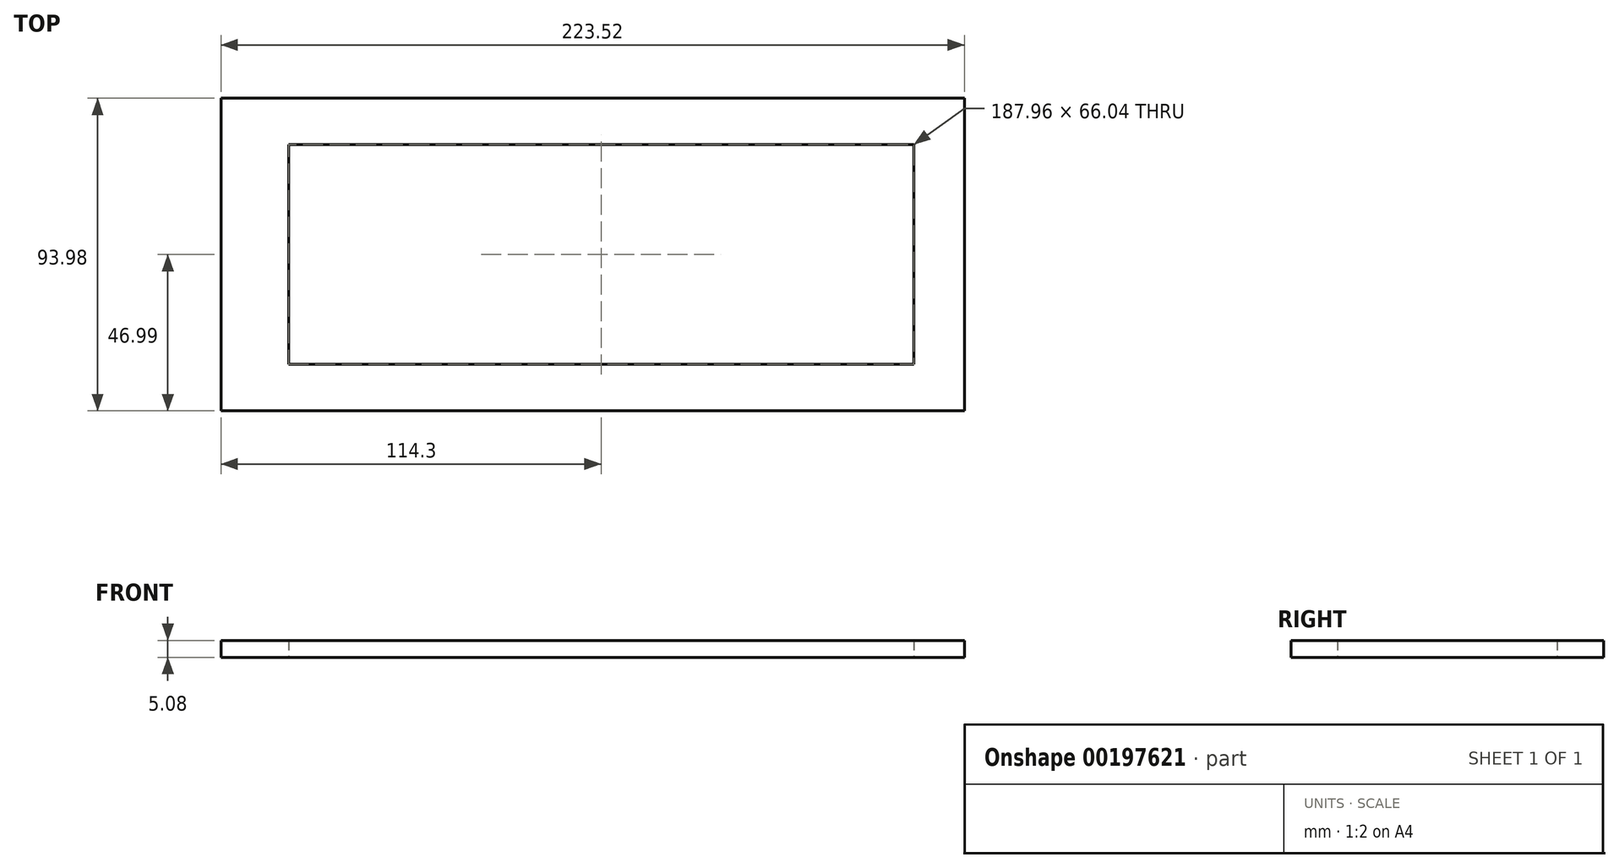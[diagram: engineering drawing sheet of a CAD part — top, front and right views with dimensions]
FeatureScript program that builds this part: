
annotation { "Feature Type Name" : "Feature", "Feature Type Description" : "" }
export const myFeature = defineFeature(function(context is Context, id is Id, definition is map)
    precondition{}
    {
        {
            var Q0;
            Q0=qCreatedBy(makeId("Top.planeOp"),FACE);
            var sketch = newSketch(context, id + "F0", { "sketchPlane" : qUnion([Q0]), "disableImprinting" : false});
            skLineSegment(sketch, "E0.bottom", {"start": v(-109.22, 47) * mm, "end": v(109.22, 47) * mm});
            skLineSegment(sketch, "E0.top", {"start": v(-109.22, -47) * mm, "end": v(109.22, -47) * mm});
            skLineSegment(sketch, "E0.right", {"start": v(109.22, 47) * mm, "end": v(109.22, -47) * mm});
            skPoint(sketch, "E0.middle", {"position": v(0, 0) * mm});
            skLineSegment(sketch, "E1", {"start": v(-109.22, 47) * mm, "end": v(-109.22, -47) * mm});
            skLineSegment(sketch, "E2.bottom", {"start": v(-93.98, 33.02) * mm, "end": v(93.98, 33.02) * mm});
            skLineSegment(sketch, "E2.top", {"start": v(-93.98, -33.02) * mm, "end": v(93.98, -33.02) * mm});
            skLineSegment(sketch, "E2.left", {"start": v(-93.98, 33.02) * mm, "end": v(-93.98, -33.02) * mm});
            skLineSegment(sketch, "E2.right", {"start": v(93.98, 33.02) * mm, "end": v(93.98, -33.02) * mm});
            skLineSegment(sketch, "E3.bottom", {"start": v(-109.22, 47) * mm, "end": v(-114.3, 47) * mm});
            skLineSegment(sketch, "E3.top", {"start": v(-109.22, -47) * mm, "end": v(-114.3, -47) * mm});
            skLineSegment(sketch, "E3.right", {"start": v(-114.3, 47) * mm, "end": v(-114.3, -47) * mm});
            skSolve(sketch);
        }
        {
            var Q0;
            Q0 = qSketchRegion(id + "F0", true);
            extrude(context, id + "F1", {"entities" : qUnion([Q0]), "depth" : 5.08 * mm});
        }
    });
